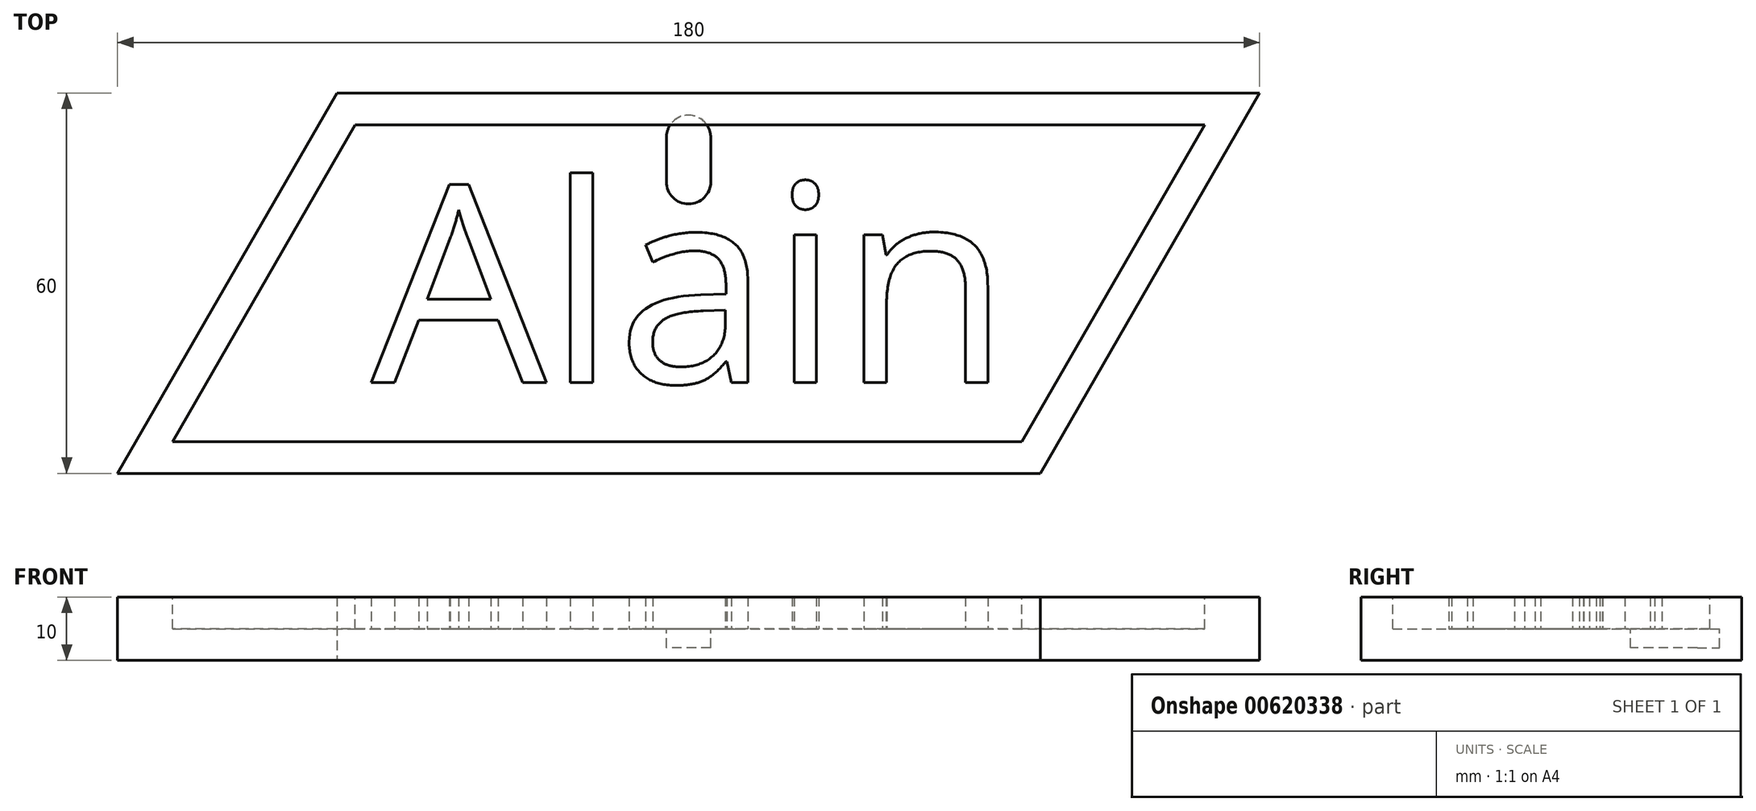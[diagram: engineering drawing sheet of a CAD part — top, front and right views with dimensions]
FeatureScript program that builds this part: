
annotation { "Feature Type Name" : "Feature", "Feature Type Description" : "" }
export const myFeature = defineFeature(function(context is Context, id is Id, definition is map)
    precondition{}
    {
        {
            var Q0;
            Q0=qCreatedBy(makeId("Top.planeOp"),FACE);
            var sketch = newSketch(context, id + "F0", { "sketchPlane" : qUnion([Q0])});
            skPoint(sketch, "E0.middle", {"position": v(0, 0) * mm});
            skLineSegment(sketch, "E1", {"start": v(-55.44, 30) * mm, "end": v(-90, -30) * mm});
            skLineSegment(sketch, "E2", {"start": v(-90, -30) * mm, "end": v(55.44, -30) * mm});
            skLineSegment(sketch, "E3", {"start": v(55.44, -30) * mm, "end": v(90, 30) * mm});
            skLineSegment(sketch, "E4", {"start": v(90, 30) * mm, "end": v(-55.44, 30) * mm});
            skPoint(sketch, "E5", {"position": v(-72.72, 0) * mm});
            skPoint(sketch, "E6", {"position": v(72.72, 0) * mm});
            skSolve(sketch);
        }
        {
            var Q0;
            Q0 = qSketchRegion(id + "F0", true);
            extrude(context, id + "F1", {"entities" : qUnion([Q0]), "depth" : 10 * mm, "offsetDistance" : 25 * mm});
        }
        {
            var Q0;
            Q0=makeQuery(id+"F1.opExtrude","CAP_FACE",FACE,{"disambiguationData":[OSD([sQuery(id+"F0.wireOp",EDGE,"E1"),sQuery(id+"F0.wireOp",EDGE,"E2"),sQuery(id+"F0.wireOp",EDGE,"E3"),sQuery(id+"F0.wireOp",EDGE,"E4")])],"isStart":false});
            var sketch = newSketch(context, id + "F2", { "sketchPlane" : qUnion([Q0])});
            skLineSegment(sketch, "E7", {"start": v(-52.55, 25) * mm, "end": v(81.35, 25) * mm});
            skLineSegment(sketch, "E8", {"start": v(81.35, 25) * mm, "end": v(52.55, -25) * mm});
            skLineSegment(sketch, "E9", {"start": v(52.55, -25) * mm, "end": v(-81.35, -25) * mm});
            skLineSegment(sketch, "E10", {"start": v(-81.35, -25) * mm, "end": v(-52.55, 25) * mm});
            skLineSegment(sketch, "E11.0", {"start": v(-55.44, 30) * mm, "end": v(-90, -30) * mm});
            skPoint(sketch, "E12.0", {"position": v(72.72, 0) * mm});
            skLineSegment(sketch, "E13.0", {"start": v(55.44, -30) * mm, "end": v(90, 30) * mm});
            skLineSegment(sketch, "E14.0", {"start": v(90, 30) * mm, "end": v(-55.44, 30) * mm});
            skLineSegment(sketch, "E15.0", {"start": v(-90, -30) * mm, "end": v(55.44, -30) * mm});
            skSolve(sketch);
        }
        {
            var Q0;
            Q0=makeQuery(id+"F2.imprint","IMPRINT",FACE,{"disambiguationData":[TD([[makeQuery(id+"F2.imprint","IMPRINT",EDGE,{"derivedFrom":sQuery(id+"F2.wireOp",EDGE,"E7")}),-1.0]])]});
            extrude(context, id + "F3", {"entities" : qUnion([Q0]), "operationType" : NewBodyOperationType.REMOVE, "oppositeDirection" : true, "depth" : 5 * mm, "offsetDistance" : 25 * mm});
        }
        {
            var Q0;
            Q0=makeQuery(id+"F3.boolean.opBoolean","COPY",FACE,{"derivedFrom":makeQuery(id+"F3.opExtrude","CAP_FACE",FACE,{"disambiguationData":[OSD([sQuery(id+"F2.wireOp",EDGE,"E7"),sQuery(id+"F2.wireOp",EDGE,"E8"),sQuery(id+"F2.wireOp",EDGE,"E9"),sQuery(id+"F2.wireOp",EDGE,"E10")])],"isStart":false})});
            var sketch = newSketch(context, id + "F4", { "sketchPlane" : qUnion([Q0])});
            skText(sketch, "E16", { "text": "Alain", "fontName": "OpenSans-Regular.ttf"});
            const initialGuessF4  = {"E16": [-0.05, -0.0157, 1, 0, 0.0314]};
            skSetInitialGuess(sketch, initialGuessF4);
            skSolve(sketch);
        }
        {
            var Q0;
            Q0 = qSketchRegion(id + "F4", true);
            extrude(context, id + "F5", {"entities" : qUnion([Q0]), "operationType" : NewBodyOperationType.ADD, "depth" : 5 * mm, "offsetDistance" : 25 * mm});
        }
        {
            var Q0;
            Q0=qCreatedBy(makeId("Top.planeOp"),FACE);
            cPlane(context, id + "F6", {"entities" : qUnion([Q0]), "cplaneType" : CPlaneType.OFFSET, "offset" : 5 * mm, "width" : 150 * mm, "height" : 150 * mm});
        }
        {
            var Q0;
            Q0=qCreatedBy(id+"F6.planeOp",FACE);
            var sketch = newSketch(context, id + "F7", { "sketchPlane" : qUnion([Q0])});
            skArc(sketch, "E17", {"start": v(3.5, 23) * mm, "mid": v(0, 26.5) * mm, "end": v(-3.5, 23) * mm});
            skArc(sketch, "E18", {"start": v(-3.5, 16) * mm, "mid": v(0, 12.5) * mm, "end": v(3.5, 16) * mm});
            skLineSegment(sketch, "E19", {"start": v(3.5, 23) * mm, "end": v(3.5, 16) * mm});
            skLineSegment(sketch, "E20", {"start": v(-3.5, 23) * mm, "end": v(-3.5, 16) * mm});
            skLineSegment(sketch, "E21.0", {"start": v(55.44, -30) * mm, "end": v(90, 30) * mm});
            skLineSegment(sketch, "E22.0", {"start": v(-55.44, 30) * mm, "end": v(-90, -30) * mm});
            skSolve(sketch);
        }
        {
            var Q0;
            Q0 = qSketchRegion(id + "F7", true);
            extrude(context, id + "F8", {"entities" : qUnion([Q0]), "operationType" : NewBodyOperationType.REMOVE, "oppositeDirection" : true, "depth" : 3 * mm, "offsetDistance" : 25 * mm});
        }
    });
